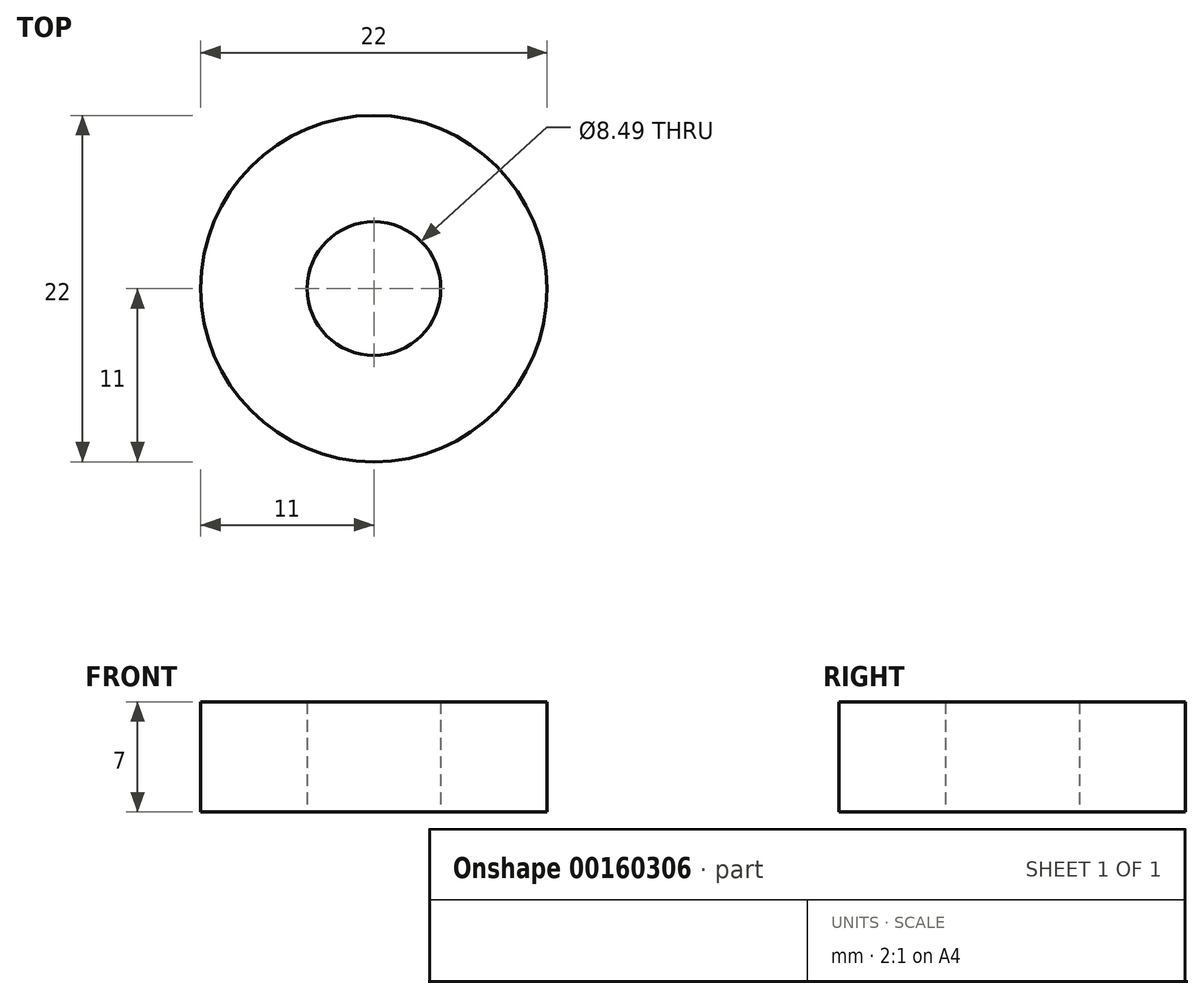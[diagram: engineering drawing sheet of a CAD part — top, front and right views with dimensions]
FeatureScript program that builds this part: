
annotation { "Feature Type Name" : "Feature", "Feature Type Description" : "" }
export const myFeature = defineFeature(function(context is Context, id is Id, definition is map)
    precondition{}
    {
        {
            var Q0;
            Q0=qCreatedBy(makeId("Top.planeOp"),FACE);
            var sketch = newSketch(context, id + "F0", { "sketchPlane" : qUnion([Q0])});
            skCircle(sketch, "E0", {"center": v(0, 0) * mm, "radius": 11 * mm});
            skCircle(sketch, "E1", {"center": v(0, 0) * mm, "radius": 4.24 * mm});
            skSolve(sketch);
        }
        {
            var Q0;
            Q0=makeQuery(id+"F0.imprint","IMPRINT",FACE,{"disambiguationData":[TD([[makeQuery(id+"F0.imprint","IMPRINT",EDGE,{"derivedFrom":sQuery(id+"F0.wireOp",EDGE,"E0")}),1.0]])]});
            extrude(context, id + "F1", {"entities" : qUnion([Q0]), "depth" : 7 * mm});
        }
    });
